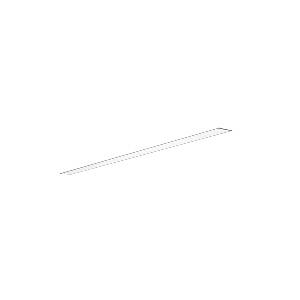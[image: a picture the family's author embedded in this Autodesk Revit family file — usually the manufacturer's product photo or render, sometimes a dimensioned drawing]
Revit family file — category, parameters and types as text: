
# Revit family: dotoo_line_-_dle_1500_830_d_00808227_e2b6
name_source: partatom
category: Lighting Fixtures
units: mm (PartAtom-declared; Revit-internal decimal feet)

## family parameters
Cut with Voids When Loaded = No
Host = Face
Light Source = No
Part Type = Normal
Room Calculation Point = No
Round Connector Dimension = Use Diameter
Shared = No

## types (1)
- DOTOO.line - DLE 1500/830/D (1 x LED, 1300 lm, 3000K)
    Apparent Load = 13 VA
    Approval mark = CE
    CIE Flux Codes = 67 91 98 100 100
    Color Rendering = 80-89
    Color Temperature = 3000K
    Control Gear = Electronic ballast
    Default Elevation = 1800 mm
    Description = DLE 1500/830/D|Recessed luminaire|light source:  |work equipment: Adjustable electronic ballast, digital DALI|connected load: 220-240 V, 50/60 Hz|Power consumption: approx. 13 W|standby: approx. 0,20|power factor: approx. 0,970|luminous flux: 1300 lm|luminous efficacy: 100 lm/W|light distribution: Direct|direct ratio: approx. 100 %|colour temperature: Warm white, ca. 3000 K|color rendering index (CRI): >= 80|chromaticity tolerance:  3 SDCM|System of protection: IP 40|class of protection: I|technology: Continuously dimmable|operation: External|luminaire body|material: Sectional aluminium|colour: White|lamp cover: Acrylic (PMMA), Clear|weight (net): approx. 3.9 kg|mains lead: Connector|Fastening: Fastening bow|glare control: Prism aperture|luminance(L65): <= 3000 cd/m|unified glare rating(4H 8H): <=  19|special features: DALI Load 1x, TouchDIM - dimming via standard switch, Flicker-free, Suitable as emergency lighting|
    Frequency = 50 Hz
    Height = 0 mm  [stored 0 ft]
    Lamp = 1 x LED
    Lamp Light Flux = 1300 lm
    Lamp count = 1
    Length = 1134 mm
    Luminous efficacy = 100 lm/W
    Manufacturer = Waldmann
    ModVariant = No
    Model = 00808227
    Mounting Place = Ceiling
    Mounting Type = Recessed
    Number of Poles = 1
    OnlyDefault = Yes
    Power Factor = 1
    Product Name = DOTOO.line - DLE 1500/830/D
    Product group = Recessed luminaire
    ProductGroupID = 4
    Protection Class = Protection class I
    Protection Degree = IP 40
    RLX_Detail_Level = 1
    RLX_Emergency_Light_Flux = 0 lm
    RLX_Emergency_Type = 0
    RLX_Emergency_Type_DB = No
    RlxData = <blob elided: 13093 chars, md5=f331a285>
    Socket = socket
    Standby Power = 0 W
    System Light Flux = 1300 lm
    System Power = 13 W
    Type Comments = Product without accessories
    Type Image = 114405000-00808223.jpg
    URL = http://relux.com
    VarID = ---
    Voltage = 230 V
    Voltage Range = 220-240 V
    Weight = 0.00 kg
    Width = 60 mm  [stored 0.19685 ft]

note: [stored X ft] marks values corroborated as IEEE doubles in the binary element streams (Revit-internal decimal feet)

## geometry (parser evidence)
native form markers: Sweep x9
no freeform markers — native parametric forms only
